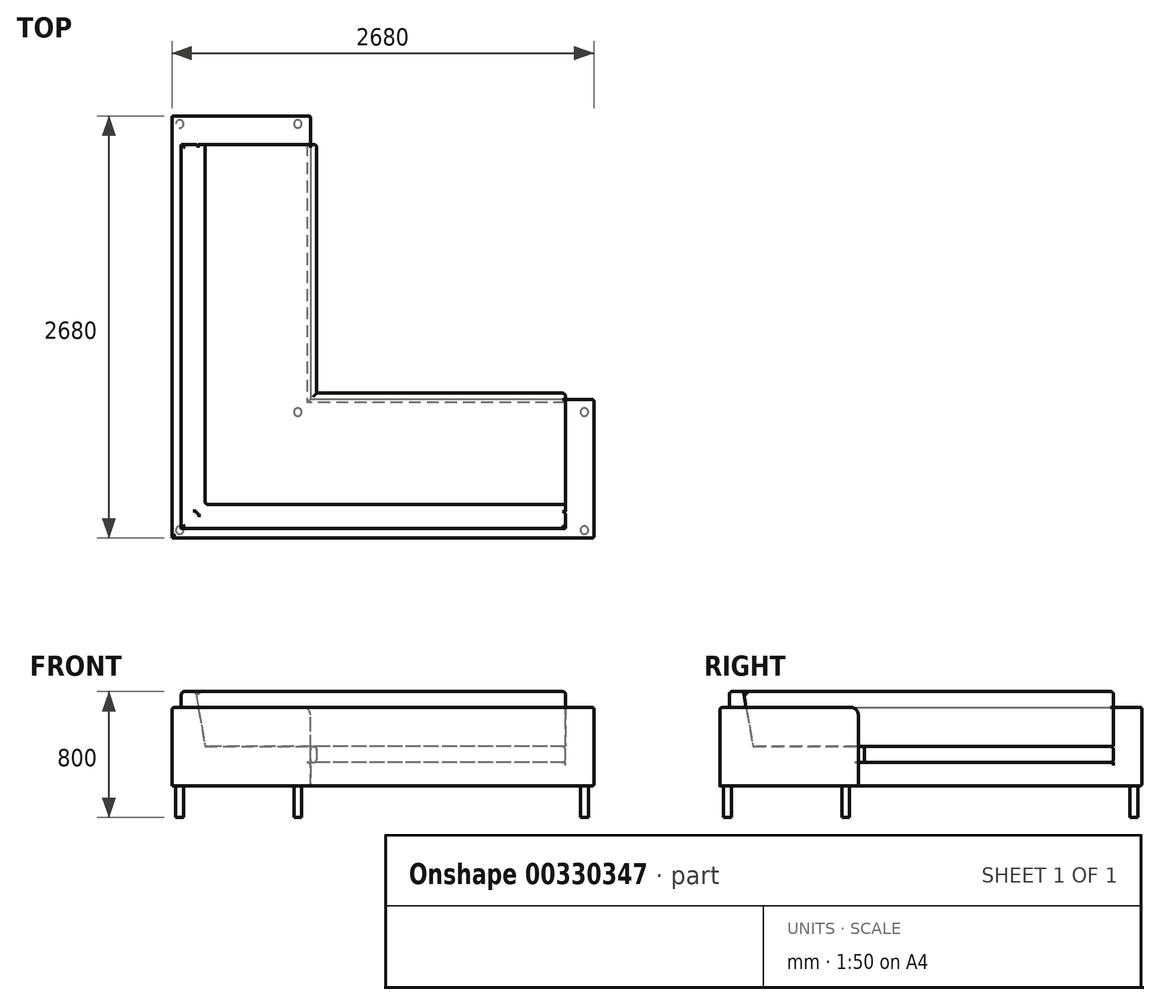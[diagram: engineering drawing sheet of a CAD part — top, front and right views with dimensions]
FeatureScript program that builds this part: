
annotation { "Feature Type Name" : "Feature", "Feature Type Description" : "" }
export const myFeature = defineFeature(function(context is Context, id is Id, definition is map)
    precondition{}
    {
        {
            var Q0;
            Q0=qCreatedBy(makeId("Front.planeOp"),FACE);
            var sketch = newSketch(context, id + "F0", { "sketchPlane" : qUnion([Q0])});
            skLineSegment(sketch, "E0", {"start": v(0, 0) * mm, "end": v(0, 600) * mm});
            skLineSegment(sketch, "E1", {"start": v(880, 130) * mm, "end": v(880, 0) * mm});
            skLineSegment(sketch, "E2", {"start": v(880, 0) * mm, "end": v(0, 0) * mm});
            skArc(sketch, "E3.filletArc", {"start": v(880, 130) * mm, "mid": v(874.14, 144.14) * mm, "end": v(860, 150) * mm});
            skLineSegment(sketch, "E4", {"start": v(0, 600) * mm, "end": v(150, 600) * mm});
            skLineSegment(sketch, "E5", {"start": v(150, 600) * mm, "end": v(211.71, 250) * mm});
            skLineSegment(sketch, "E6", {"start": v(211.71, 250) * mm, "end": v(920, 250) * mm});
            skLineSegment(sketch, "E7.bottom", {"start": v(860, 150) * mm, "end": v(920, 150) * mm});
            skLineSegment(sketch, "E7.right", {"start": v(920, 150) * mm, "end": v(920, 250) * mm});
            skSolve(sketch);
        }
        {
            var Q0;
            Q0=qSketchRegion(id+"F0",true);
            extrude(context, id + "F1", {"entities" : qUnion([Q0]), "oppositeDirection" : true, "depth" : 2500 * mm});
        }
        {
            var Q0;
            Q0=qCreatedBy(makeId("Right.planeOp"),FACE);
            var sketch = newSketch(context, id + "F2", { "sketchPlane" : qUnion([Q0])});
            skLineSegment(sketch, "E8", {"start": v(0, 0) * mm, "end": v(0, 600) * mm});
            skLineSegment(sketch, "E9", {"start": v(880, 130) * mm, "end": v(880, 0) * mm});
            skLineSegment(sketch, "E10", {"start": v(880, 0) * mm, "end": v(0, 0) * mm});
            skArc(sketch, "E11.filletArc", {"start": v(880, 130) * mm, "mid": v(874.14, 144.14) * mm, "end": v(860, 150) * mm});
            skLineSegment(sketch, "E12", {"start": v(0, 600) * mm, "end": v(150, 600) * mm});
            skLineSegment(sketch, "E13", {"start": v(150, 600) * mm, "end": v(211.71, 250) * mm});
            skLineSegment(sketch, "E14", {"start": v(211.71, 250) * mm, "end": v(920, 250) * mm});
            skLineSegment(sketch, "E15.bottom", {"start": v(860, 150) * mm, "end": v(920, 150) * mm});
            skLineSegment(sketch, "E15.right", {"start": v(920, 150) * mm, "end": v(920, 250) * mm});
            skSolve(sketch);
        }
        {
            var Q0;
            Q0=qSketchRegion(id+"F2",true);
            extrude(context, id + "F3", {"entities" : qUnion([Q0]), "operationType" : NewBodyOperationType.ADD, "depth" : 2500 * mm});
        }
        {
            var Q0;
            Q0=makeQuery(id+"F3.opExtrude","CAP_FACE",FACE,{"disambiguationData":[OSD([sQuery(id+"F2.wireOp",EDGE,"E8"),sQuery(id+"F2.wireOp",EDGE,"E9"),sQuery(id+"F2.wireOp",EDGE,"E10"),sQuery(id+"F2.wireOp",EDGE,"E11.filletArc"),sQuery(id+"F2.wireOp",EDGE,"E12"),sQuery(id+"F2.wireOp",EDGE,"E13"),sQuery(id+"F2.wireOp",EDGE,"E14"),sQuery(id+"F2.wireOp",EDGE,"E15.bottom"),sQuery(id+"F2.wireOp",EDGE,"E15.right")])],"isStart":false});
            var sketch = newSketch(context, id + "F4", { "sketchPlane" : qUnion([Q0])});
            skLineSegment(sketch, "E16.bottom", {"start": v(-100, 650) * mm, "end": v(60, 650) * mm});
            skLineSegment(sketch, "E16.top", {"start": v(-100, 500) * mm, "end": v(60, 500) * mm});
            skLineSegment(sketch, "E16.left", {"start": v(-100, 650) * mm, "end": v(-100, 500) * mm});
            skLineSegment(sketch, "E16.right", {"start": v(60, 650) * mm, "end": v(60, 500) * mm});
            skSolve(sketch);
        }
        {
            var Q0;
            Q0=qSketchRegion(id+"F4",true);
            extrude(context, id + "F5", {"entities" : qUnion([Q0]), "operationType" : NewBodyOperationType.REMOVE, "endBound" : BoundingType.THROUGH_ALL, "oppositeDirection" : true, "depth" : 25 * mm});
        }
        {
            var Q0;
            Q0=makeQuery(id+"F1.opExtrude","CAP_FACE",FACE,{"disambiguationData":[OSD([sQuery(id+"F0.wireOp",EDGE,"E0"),sQuery(id+"F0.wireOp",EDGE,"E1"),sQuery(id+"F0.wireOp",EDGE,"E2"),sQuery(id+"F0.wireOp",EDGE,"E3.filletArc"),sQuery(id+"F0.wireOp",EDGE,"E4"),sQuery(id+"F0.wireOp",EDGE,"E5"),sQuery(id+"F0.wireOp",EDGE,"E6"),sQuery(id+"F0.wireOp",EDGE,"E7.bottom"),sQuery(id+"F0.wireOp",EDGE,"E7.right")])],"isStart":false});
            var sketch = newSketch(context, id + "F6", { "sketchPlane" : qUnion([Q0])});
            skLineSegment(sketch, "E17.bottom", {"start": v(90, 650) * mm, "end": v(-60, 650) * mm});
            skLineSegment(sketch, "E17.top", {"start": v(90, 500) * mm, "end": v(-60, 500) * mm});
            skLineSegment(sketch, "E17.left", {"start": v(90, 650) * mm, "end": v(90, 500) * mm});
            skLineSegment(sketch, "E17.right", {"start": v(-60, 650) * mm, "end": v(-60, 500) * mm});
            skSolve(sketch);
        }
        {
            var Q0;
            Q0=qSketchRegion(id+"F6",true);
            extrude(context, id + "F7", {"entities" : qUnion([Q0]), "operationType" : NewBodyOperationType.REMOVE, "endBound" : BoundingType.THROUGH_ALL, "oppositeDirection" : true, "depth" : 25 * mm});
        }
        {
            var Q0;
            Q0=makeQuery(id+"F3.opExtrude","CAP_FACE",FACE,{"disambiguationData":[OSD([sQuery(id+"F2.wireOp",EDGE,"E8"),sQuery(id+"F2.wireOp",EDGE,"E9"),sQuery(id+"F2.wireOp",EDGE,"E10"),sQuery(id+"F2.wireOp",EDGE,"E11.filletArc"),sQuery(id+"F2.wireOp",EDGE,"E12"),sQuery(id+"F2.wireOp",EDGE,"E13"),sQuery(id+"F2.wireOp",EDGE,"E14"),sQuery(id+"F2.wireOp",EDGE,"E15.bottom"),sQuery(id+"F2.wireOp",EDGE,"E15.right")])],"isStart":false});
            var sketch = newSketch(context, id + "F8", { "sketchPlane" : qUnion([Q0])});
            skLineSegment(sketch, "E18.bottom", {"start": v(0, 0) * mm, "end": v(880, 0) * mm});
            skLineSegment(sketch, "E18.top", {"start": v(0, 500) * mm, "end": v(880, 500) * mm});
            skLineSegment(sketch, "E18.left", {"start": v(0, 0) * mm, "end": v(0, 500) * mm});
            skLineSegment(sketch, "E18.right", {"start": v(880, 0) * mm, "end": v(880, 500) * mm});
            skSolve(sketch);
        }
        {
            var Q0;
            Q0=qSketchRegion(id+"F8",true);
            extrude(context, id + "F9", {"entities" : qUnion([Q0]), "operationType" : NewBodyOperationType.ADD, "depth" : 180 * mm});
        }
        {
            var Q0;
            Q0=makeQuery(id+"F1.opExtrude","CAP_FACE",FACE,{"disambiguationData":[OSD([sQuery(id+"F0.wireOp",EDGE,"E0"),sQuery(id+"F0.wireOp",EDGE,"E1"),sQuery(id+"F0.wireOp",EDGE,"E2"),sQuery(id+"F0.wireOp",EDGE,"E3.filletArc"),sQuery(id+"F0.wireOp",EDGE,"E4"),sQuery(id+"F0.wireOp",EDGE,"E5"),sQuery(id+"F0.wireOp",EDGE,"E6"),sQuery(id+"F0.wireOp",EDGE,"E7.bottom"),sQuery(id+"F0.wireOp",EDGE,"E7.right")])],"isStart":false});
            var sketch = newSketch(context, id + "F10", { "sketchPlane" : qUnion([Q0])});
            skLineSegment(sketch, "E19.bottom", {"start": v(0, 0) * mm, "end": v(-880, 0) * mm});
            skLineSegment(sketch, "E19.top", {"start": v(0, 500) * mm, "end": v(-880, 500) * mm});
            skLineSegment(sketch, "E19.left", {"start": v(0, 0) * mm, "end": v(0, 500) * mm});
            skLineSegment(sketch, "E19.right", {"start": v(-880, 0) * mm, "end": v(-880, 500) * mm});
            skSolve(sketch);
        }
        {
            var Q0;
            Q0=qSketchRegion(id+"F10",true);
            extrude(context, id + "F11", {"entities" : qUnion([Q0]), "operationType" : NewBodyOperationType.ADD, "depth" : 180 * mm});
        }
        {
            var Q0;
            Q0=makeQuery(id+"F3.opExtrude","SWEPT_EDGE",EDGE,{"disambiguationData":[OSD([sQuery(id+"F2.wireOp",EDGE,"E12"),sQuery(id+"F2.wireOp",EDGE,"E13")])]});
            var Q1;
            Q1=makeQuery(id+"F5.boolean.opBoolean","INTERSECT",EDGE,{"derivedFrom":[makeQuery(id+"F3.boolean.opBoolean","MERGE",FACE,{"derivedFrom":[makeQuery(id+"F1.opExtrude","SWEPT_FACE",FACE,{"disambiguationData":[OSD([sQuery(id+"F0.wireOp",EDGE,"E4")])]}),makeQuery(id+"F3.opExtrude","SWEPT_FACE",FACE,{"disambiguationData":[OSD([sQuery(id+"F2.wireOp",EDGE,"E12")])]})]}),makeQuery(id+"F5.opExtrude","SWEPT_FACE",FACE,{"disambiguationData":[OSD([sQuery(id+"F4.wireOp",EDGE,"E16.right")])]})]});
            var Q2;
            Q2=makeQuery(id+"F3.opExtrude","SWEPT_EDGE",EDGE,{"disambiguationData":[OSD([sQuery(id+"F2.wireOp",EDGE,"E14"),sQuery(id+"F2.wireOp",EDGE,"E15.right")])]});
            var Q3;
            Q3=makeQuery(id+"F1.opExtrude","SWEPT_EDGE",EDGE,{"disambiguationData":[OSD([sQuery(id+"F0.wireOp",EDGE,"E6"),sQuery(id+"F0.wireOp",EDGE,"E7.right")])]});
            var Q4;
            Q4=makeQuery(id+"F3.opExtrude","SWEPT_EDGE",EDGE,{"disambiguationData":[OSD([sQuery(id+"F2.wireOp",EDGE,"E15.bottom"),sQuery(id+"F2.wireOp",EDGE,"E15.right")])]});
            var Q5;
            Q5=makeQuery(id+"F1.opExtrude","SWEPT_EDGE",EDGE,{"disambiguationData":[OSD([sQuery(id+"F0.wireOp",EDGE,"E7.bottom"),sQuery(id+"F0.wireOp",EDGE,"E7.right")])]});
            var Q6;
            Q6=makeQuery(id+"F1.opExtrude","SWEPT_EDGE",EDGE,{"disambiguationData":[OSD([sQuery(id+"F0.wireOp",EDGE,"E4"),sQuery(id+"F0.wireOp",EDGE,"E5")])]});
            var Q7;
            Q7=makeQuery(id+"F7.boolean.opBoolean","INTERSECT",EDGE,{"derivedFrom":[makeQuery(id+"F3.boolean.opBoolean","MERGE",FACE,{"derivedFrom":[makeQuery(id+"F1.opExtrude","SWEPT_FACE",FACE,{"disambiguationData":[OSD([sQuery(id+"F0.wireOp",EDGE,"E4")])]}),makeQuery(id+"F3.opExtrude","SWEPT_FACE",FACE,{"disambiguationData":[OSD([sQuery(id+"F2.wireOp",EDGE,"E12")])]})]}),makeQuery(id+"F7.opExtrude","SWEPT_FACE",FACE,{"disambiguationData":[OSD([sQuery(id+"F6.wireOp",EDGE,"E17.right")])]})]});
            var Q8;
            Q8=makeQuery(id+"F5.boolean.opBoolean","INTERSECT",EDGE,{"derivedFrom":[makeQuery(id+"F3.boolean.opBoolean","MERGE",FACE,{"derivedFrom":[makeQuery(id+"F1.opExtrude","CAP_FACE",FACE,{"disambiguationData":[OSD([sQuery(id+"F0.wireOp",EDGE,"E0"),sQuery(id+"F0.wireOp",EDGE,"E1"),sQuery(id+"F0.wireOp",EDGE,"E2"),sQuery(id+"F0.wireOp",EDGE,"E3.filletArc"),sQuery(id+"F0.wireOp",EDGE,"E4"),sQuery(id+"F0.wireOp",EDGE,"E5"),sQuery(id+"F0.wireOp",EDGE,"E6"),sQuery(id+"F0.wireOp",EDGE,"E7.bottom"),sQuery(id+"F0.wireOp",EDGE,"E7.right")])],"isStart":true}),makeQuery(id+"F3.opExtrude","SWEPT_FACE",FACE,{"disambiguationData":[OSD([sQuery(id+"F2.wireOp",EDGE,"E8")])]})]}),makeQuery(id+"F5.opExtrude","SWEPT_FACE",FACE,{"disambiguationData":[OSD([sQuery(id+"F4.wireOp",EDGE,"E16.top")])]})]});
            var Q9;
            Q9=makeQuery(id+"F7.boolean.opBoolean","INTERSECT",EDGE,{"derivedFrom":[makeQuery(id+"F1.opExtrude","SWEPT_FACE",FACE,{"disambiguationData":[OSD([sQuery(id+"F0.wireOp",EDGE,"E0")])]}),makeQuery(id+"F7.opExtrude","SWEPT_FACE",FACE,{"disambiguationData":[OSD([sQuery(id+"F6.wireOp",EDGE,"E17.top")])]})]});
            var Q10;
            Q10=makeQuery(id+"F3.opExtrude","CAP_EDGE",EDGE,{"disambiguationData":[OSD([sQuery(id+"F2.wireOp",EDGE,"E15.right")])],"isStart":false});
            var Q11;
            {var subQ0=sQuery(id+"F2.wireOp",EDGE,"E14");Q11=makeQuery(id+"F9.boolean.opBoolean","SPLIT",EDGE,{"disambiguationData":[topologyDisambiguationEdgeConnected([makeQuery(id+"F3.opExtrude","CAP_FACE",FACE,{"disambiguationData":[OSD([sQuery(id+"F2.wireOp",EDGE,"E8"),sQuery(id+"F2.wireOp",EDGE,"E9"),sQuery(id+"F2.wireOp",EDGE,"E10"),sQuery(id+"F2.wireOp",EDGE,"E11.filletArc"),sQuery(id+"F2.wireOp",EDGE,"E12"),sQuery(id+"F2.wireOp",EDGE,"E13"),subQ0,sQuery(id+"F2.wireOp",EDGE,"E15.bottom"),sQuery(id+"F2.wireOp",EDGE,"E15.right")])],"isStart":false})])],"derivedFrom":makeQuery(id+"F3.opExtrude","CAP_EDGE",EDGE,{"disambiguationData":[OSD([subQ0])],"isStart":false})});}
            var Q12;
            {var subQ0=sQuery(id+"F2.wireOp",EDGE,"E15.bottom");Q12=makeQuery(id+"F9.boolean.opBoolean","SPLIT",EDGE,{"disambiguationData":[topologyDisambiguationEdgeConnected([makeQuery(id+"F3.opExtrude","CAP_FACE",FACE,{"disambiguationData":[OSD([sQuery(id+"F2.wireOp",EDGE,"E8"),sQuery(id+"F2.wireOp",EDGE,"E9"),sQuery(id+"F2.wireOp",EDGE,"E10"),sQuery(id+"F2.wireOp",EDGE,"E11.filletArc"),sQuery(id+"F2.wireOp",EDGE,"E12"),sQuery(id+"F2.wireOp",EDGE,"E13"),sQuery(id+"F2.wireOp",EDGE,"E14"),subQ0,sQuery(id+"F2.wireOp",EDGE,"E15.right")])],"isStart":false})])],"derivedFrom":makeQuery(id+"F3.opExtrude","CAP_EDGE",EDGE,{"disambiguationData":[OSD([subQ0])],"isStart":false})});}
            var Q13;
            {var subQ0=sQuery(id+"F0.wireOp",EDGE,"E6");Q13=makeQuery(id+"F11.boolean.opBoolean","SPLIT",EDGE,{"disambiguationData":[topologyDisambiguationEdgeConnected([makeQuery(id+"F1.opExtrude","CAP_FACE",FACE,{"disambiguationData":[OSD([sQuery(id+"F0.wireOp",EDGE,"E0"),sQuery(id+"F0.wireOp",EDGE,"E1"),sQuery(id+"F0.wireOp",EDGE,"E2"),sQuery(id+"F0.wireOp",EDGE,"E3.filletArc"),sQuery(id+"F0.wireOp",EDGE,"E4"),sQuery(id+"F0.wireOp",EDGE,"E5"),subQ0,sQuery(id+"F0.wireOp",EDGE,"E7.bottom"),sQuery(id+"F0.wireOp",EDGE,"E7.right")])],"isStart":false})])],"derivedFrom":makeQuery(id+"F1.opExtrude","CAP_EDGE",EDGE,{"disambiguationData":[OSD([subQ0])],"isStart":false})});}
            var Q14;
            Q14=makeQuery(id+"F1.opExtrude","CAP_EDGE",EDGE,{"disambiguationData":[OSD([sQuery(id+"F0.wireOp",EDGE,"E7.right")])],"isStart":false});
            var Q15;
            {var subQ0=sQuery(id+"F0.wireOp",EDGE,"E7.bottom");Q15=makeQuery(id+"F11.boolean.opBoolean","SPLIT",EDGE,{"disambiguationData":[topologyDisambiguationEdgeConnected([makeQuery(id+"F1.opExtrude","CAP_FACE",FACE,{"disambiguationData":[OSD([sQuery(id+"F0.wireOp",EDGE,"E0"),sQuery(id+"F0.wireOp",EDGE,"E1"),sQuery(id+"F0.wireOp",EDGE,"E2"),sQuery(id+"F0.wireOp",EDGE,"E3.filletArc"),sQuery(id+"F0.wireOp",EDGE,"E4"),sQuery(id+"F0.wireOp",EDGE,"E5"),sQuery(id+"F0.wireOp",EDGE,"E6"),subQ0,sQuery(id+"F0.wireOp",EDGE,"E7.right")])],"isStart":false})])],"derivedFrom":makeQuery(id+"F1.opExtrude","CAP_EDGE",EDGE,{"disambiguationData":[OSD([subQ0])],"isStart":false})});}
            var Q16;
            Q16=makeQuery(id+"F7.boolean.opBoolean","COPY",EDGE,{"derivedFrom":makeQuery(id+"F7.opExtrude","CAP_EDGE",EDGE,{"disambiguationData":[OSD([sQuery(id+"F6.wireOp",EDGE,"E17.right")])],"isStart":true})});
            var Q17;
            Q17=makeQuery(id+"F1.opExtrude","CAP_EDGE",EDGE,{"disambiguationData":[OSD([sQuery(id+"F0.wireOp",EDGE,"E4")])],"isStart":false});
            var Q18;
            {var subQ0=sQuery(id+"F0.wireOp",EDGE,"E5");Q18=makeQuery(id+"F11.boolean.opBoolean","SPLIT",EDGE,{"disambiguationData":[topologyDisambiguationEdgeConnected([makeQuery(id+"F1.opExtrude","CAP_FACE",FACE,{"disambiguationData":[OSD([sQuery(id+"F0.wireOp",EDGE,"E0"),sQuery(id+"F0.wireOp",EDGE,"E1"),sQuery(id+"F0.wireOp",EDGE,"E2"),sQuery(id+"F0.wireOp",EDGE,"E3.filletArc"),sQuery(id+"F0.wireOp",EDGE,"E4"),subQ0,sQuery(id+"F0.wireOp",EDGE,"E6"),sQuery(id+"F0.wireOp",EDGE,"E7.bottom"),sQuery(id+"F0.wireOp",EDGE,"E7.right")])],"isStart":false})])],"derivedFrom":makeQuery(id+"F1.opExtrude","CAP_EDGE",EDGE,{"disambiguationData":[OSD([subQ0])],"isStart":false})});}
            var Q19;
            Q19=makeQuery(id+"F5.boolean.opBoolean","COPY",EDGE,{"derivedFrom":makeQuery(id+"F5.opExtrude","CAP_EDGE",EDGE,{"disambiguationData":[OSD([sQuery(id+"F4.wireOp",EDGE,"E16.right")])],"isStart":true})});
            var Q20;
            Q20=makeQuery(id+"F3.opExtrude","CAP_EDGE",EDGE,{"disambiguationData":[OSD([sQuery(id+"F2.wireOp",EDGE,"E12")])],"isStart":false});
            var Q21;
            {var subQ0=sQuery(id+"F2.wireOp",EDGE,"E13");Q21=makeQuery(id+"F9.boolean.opBoolean","SPLIT",EDGE,{"disambiguationData":[topologyDisambiguationEdgeConnected([makeQuery(id+"F3.opExtrude","CAP_FACE",FACE,{"disambiguationData":[OSD([sQuery(id+"F2.wireOp",EDGE,"E8"),sQuery(id+"F2.wireOp",EDGE,"E9"),sQuery(id+"F2.wireOp",EDGE,"E10"),sQuery(id+"F2.wireOp",EDGE,"E11.filletArc"),sQuery(id+"F2.wireOp",EDGE,"E12"),subQ0,sQuery(id+"F2.wireOp",EDGE,"E14"),sQuery(id+"F2.wireOp",EDGE,"E15.bottom"),sQuery(id+"F2.wireOp",EDGE,"E15.right")])],"isStart":false})])],"derivedFrom":makeQuery(id+"F3.opExtrude","CAP_EDGE",EDGE,{"disambiguationData":[OSD([subQ0])],"isStart":false})});}
            var Q22;
            Q22=makeQuery(id+"F3.boolean.opBoolean","INTERSECT",EDGE,{"derivedFrom":[makeQuery(id+"F1.opExtrude","SWEPT_FACE",FACE,{"disambiguationData":[OSD([sQuery(id+"F0.wireOp",EDGE,"E5")])]}),makeQuery(id+"F3.opExtrude","SWEPT_FACE",FACE,{"disambiguationData":[OSD([sQuery(id+"F2.wireOp",EDGE,"E13")])]})]});
            fillet(context, id + "F12", {"entities" : qUnion([Q0, Q1, Q2, Q3, Q4, Q5, Q6, Q7, Q8, Q9, Q10, Q11, Q12, Q13, Q14, Q15, Q16, Q17, Q18, Q19, Q20, Q21, Q22]), "radius" : 20 * mm, "tangentPropagation" : true, "allowEdgeOverflow" : false});
        }
        {
            var Q0;
            Q0=makeQuery(id+"F9.opExtrude","SWEPT_EDGE",EDGE,{"disambiguationData":[OSD([sQuery(id+"F8.wireOp",EDGE,"E18.top"),sQuery(id+"F8.wireOp",EDGE,"E18.right")])]});
            var Q1;
            Q1=makeQuery(id+"F11.opExtrude","SWEPT_EDGE",EDGE,{"disambiguationData":[OSD([sQuery(id+"F10.wireOp",EDGE,"E19.top"),sQuery(id+"F10.wireOp",EDGE,"E19.right")])]});
            fillet(context, id + "F13", {"entities" : qUnion([Q0, Q1]), "radius" : 50 * mm, "tangentPropagation" : true, "allowEdgeOverflow" : false});
        }
        {
            var Q0;
            Q0=makeQuery(id+"F9.opExtrude","CAP_FACE",FACE,{"disambiguationData":[OSD([sQuery(id+"F8.wireOp",EDGE,"E18.bottom"),sQuery(id+"F8.wireOp",EDGE,"E18.top"),sQuery(id+"F8.wireOp",EDGE,"E18.left"),sQuery(id+"F8.wireOp",EDGE,"E18.right")])],"isStart":false});
            var Q1;
            Q1=makeQuery(id+"F11.opExtrude","CAP_FACE",FACE,{"disambiguationData":[OSD([sQuery(id+"F10.wireOp",EDGE,"E19.bottom"),sQuery(id+"F10.wireOp",EDGE,"E19.top"),sQuery(id+"F10.wireOp",EDGE,"E19.left"),sQuery(id+"F10.wireOp",EDGE,"E19.right")])],"isStart":false});
            fillet(context, id + "F14", {"entities" : qUnion([Q0, Q1]), "radius" : 10 * mm, "tangentPropagation" : true, "allowEdgeOverflow" : false});
        }
        {
            var Q0;
            Q0=makeQuery(id+"F11.boolean.opBoolean","MERGE",FACE,{"derivedFrom":[makeQuery(id+"F9.boolean.opBoolean","MERGE",FACE,{"derivedFrom":[makeQuery(id+"F3.boolean.opBoolean","MERGE",FACE,{"derivedFrom":[makeQuery(id+"F1.opExtrude","SWEPT_FACE",FACE,{"disambiguationData":[OSD([sQuery(id+"F0.wireOp",EDGE,"E2")])]}),makeQuery(id+"F3.opExtrude","SWEPT_FACE",FACE,{"disambiguationData":[OSD([sQuery(id+"F2.wireOp",EDGE,"E10")])]})]}),makeQuery(id+"F9.opExtrude","SWEPT_FACE",FACE,{"disambiguationData":[OSD([sQuery(id+"F8.wireOp",EDGE,"E18.bottom")])]})]}),makeQuery(id+"F11.opExtrude","SWEPT_FACE",FACE,{"disambiguationData":[OSD([sQuery(id+"F10.wireOp",EDGE,"E19.bottom")])]})]});
            var sketch = newSketch(context, id + "F15", { "sketchPlane" : qUnion([Q0])});
            skCircle(sketch, "E20", {"center": v(50, -2630) * mm, "radius": 25 * mm});
            skCircle(sketch, "E21.0.1.0", {"center": v(50, -50) * mm, "radius": 25 * mm});
            skCircle(sketch, "E21.1.0.0", {"center": v(800, -2630) * mm, "radius": 25 * mm});
            skLineSegment(sketch, "E21.direction1", {"start": v(50, -2630) * mm, "end": v(800, -2630) * mm, "construction": true});
            skLineSegment(sketch, "E21.direction2", {"start": v(50, -2630) * mm, "end": v(50, -50) * mm, "construction": true});
            skCircle(sketch, "E22.1.0.0", {"center": v(2620, -50) * mm, "radius": 25 * mm});
            skCircle(sketch, "E22.1.1.0", {"center": v(2620, -800) * mm, "radius": 25 * mm});
            skLineSegment(sketch, "E22.direction1", {"start": v(50, -50) * mm, "end": v(2620, -50) * mm, "construction": true});
            skLineSegment(sketch, "E22.direction2", {"start": v(50, -50) * mm, "end": v(50, -830) * mm, "construction": true});
            skCircle(sketch, "E23", {"center": v(800, -800) * mm, "radius": 25 * mm});
            skLineSegment(sketch, "E24", {"start": v(800, -2630) * mm, "end": v(800, -800) * mm, "construction": true});
            skLineSegment(sketch, "E25", {"start": v(800, -800) * mm, "end": v(2620, -800) * mm, "construction": true});
            skLineSegment(sketch, "E26", {"start": v(2620, -50) * mm, "end": v(2620, -800) * mm, "construction": true});
            skSolve(sketch);
        }
        {
            var Q0;
            Q0=qSketchRegion(id+"F15",true);
            extrude(context, id + "F16", {"entities" : qUnion([Q0]), "operationType" : NewBodyOperationType.ADD, "depth" : 200 * mm});
        }
    });
